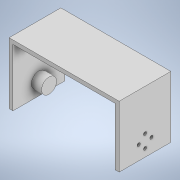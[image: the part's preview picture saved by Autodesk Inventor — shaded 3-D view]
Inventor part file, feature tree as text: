
AUTODESK INVENTOR PART (.ipt)
format: ipt  version: 2022 (Build 260153000, 153)  size: 131,584 bytes
history: native  units: mm
features: extrude x4, sketch x4
ambient origin geometry x8: Origin, YZ Plane, XZ Plane, XY Plane, X Axis, Y Axis, Z Axis, Center Point
bodies: Solid1 (feature_tree)
feature tree (8):
  extrude  "Extrusion1"  Depth=80.0mm
  extrude  "Extrusion2"  Depth=48.0mm
  extrude  "Extrusion3"  Depth=40.4mm TaperAngle=0.0deg
  extrude  "Extrusion4"  Depth=1.0mm TaperAngle=360.0deg
  sketch  "Sketch1"  dims[d0=45.0mm d1=80.0mm]
  sketch  "Sketch2"  dims[d2=3.0mm d3=48.0mm]
  sketch  "Sketch3"  dims[d4=86.0mm d5=40.4mm d6=0.0mm]
  sketch  "Sketch4"  dims[d9=2.5mm d10=40.0mm d12=360.0deg d14=40.4mm d15=0.0mm d17=11.75mm d18=8.0mm d19=0.0mm d20=16.0mm d21=1.0mm d22=0.0mm]
